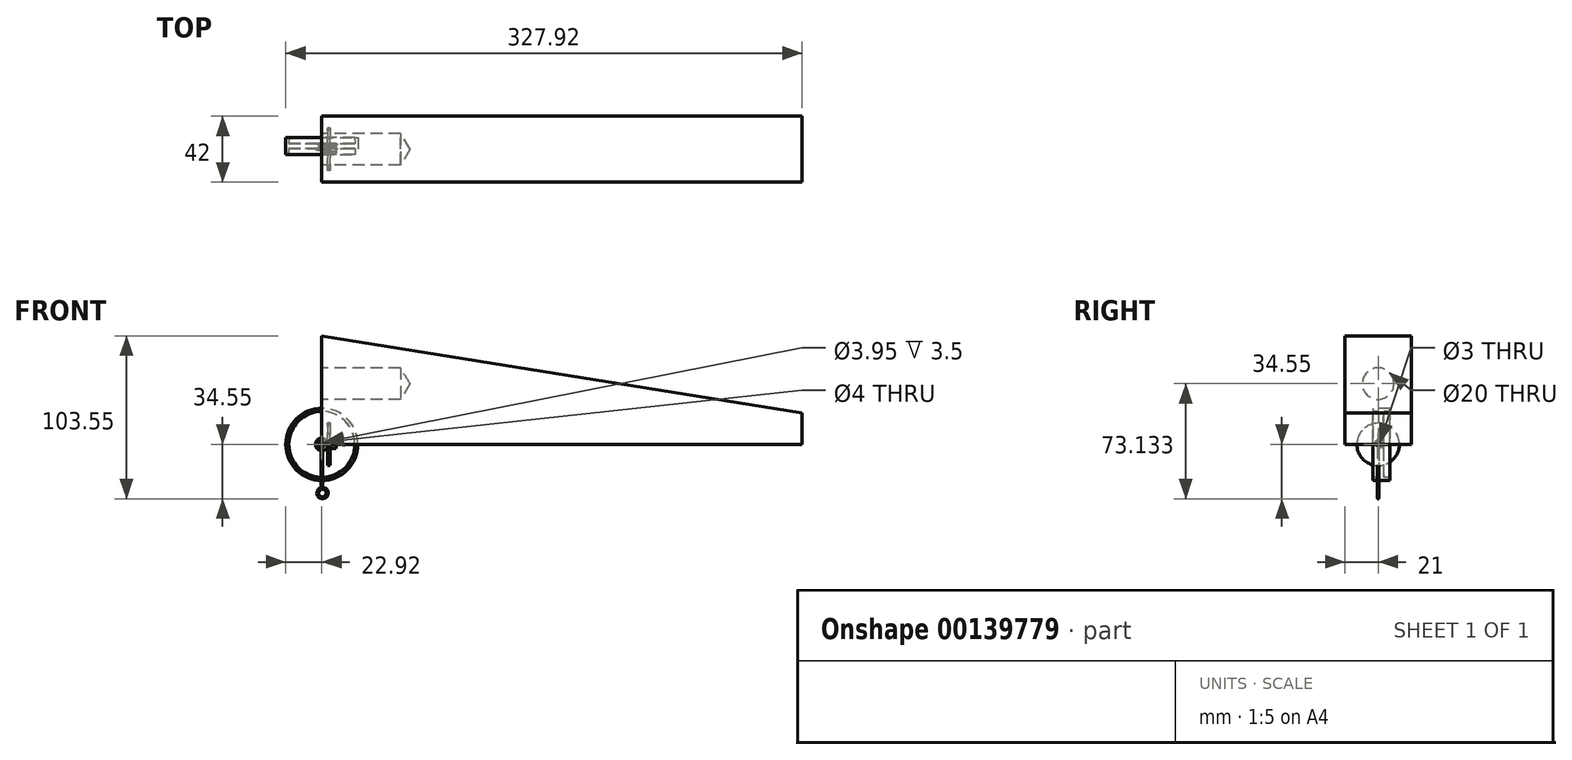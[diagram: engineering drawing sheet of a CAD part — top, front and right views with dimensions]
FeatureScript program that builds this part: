
annotation { "Feature Type Name" : "Feature", "Feature Type Description" : "" }
export const myFeature = defineFeature(function(context is Context, id is Id, definition is map)
    precondition{}
    {
        {
            var Q0;
            Q0=qCreatedBy(makeId("Front.planeOp"),FACE);
            var sketch = newSketch(context, id + "F0", { "sketchPlane" : qUnion([Q0])});
            skLineSegment(sketch, "E0", {"start": v(0, 0) * mm, "end": v(305, 0) * mm});
            skLineSegment(sketch, "E1", {"start": v(305, 0) * mm, "end": v(305, 20) * mm});
            skLineSegment(sketch, "E2", {"start": v(305, 20) * mm, "end": v(0, 69) * mm});
            skLineSegment(sketch, "E3", {"start": v(0, 69) * mm, "end": v(0, 0) * mm});
            skSolve(sketch);
        }
        {
            var Q0;
            Q0=qSketchRegion(id+"F0",true);
            extrude(context, id + "F1", {"entities" : qUnion([Q0]), "endBound" : BoundingType.SYMMETRIC, "depth" : 42 * mm});
        }
        {
            var Q0;
            Q0=qCreatedBy(makeId("Front.planeOp"),FACE);
            var sketch = newSketch(context, id + "F2", { "sketchPlane" : qUnion([Q0])});
            skCircle(sketch, "E4", {"center": v(0, 0) * mm, "radius": 4 * mm});
            skCircle(sketch, "E5", {"center": v(0, 0) * mm, "radius": 2 * mm});
            skSolve(sketch);
        }
        {
            var Q0;
            Q0=makeQuery(id+"F2.imprint","IMPRINT",FACE,{"disambiguationData":[TD([[makeQuery(id+"F2.imprint","IMPRINT",EDGE,{"derivedFrom":sQuery(id+"F2.wireOp",EDGE,"E4")}),1.0]])]});
            extrude(context, id + "F3", {"entities" : qUnion([Q0]), "endBound" : BoundingType.SYMMETRIC, "depth" : .33333333333333331968 * mm});
        }
        {
            var Q0;
            Q0=qCreatedBy(makeId("Right.planeOp"),FACE);
            var sketch = newSketch(context, id + "F4", { "sketchPlane" : qUnion([Q0])});
            skLineSegment(sketch, "E6", {"start": v(0, 0) * mm, "end": v(4.06, 0) * mm, "construction": true});
            skLineSegment(sketch, "E7", {"start": v(0, 1.98) * mm, "end": v(3.5, 1.98) * mm});
            skLineSegment(sketch, "E8", {"start": v(3.5, 1.98) * mm, "end": v(3.5, 2.98) * mm});
            skLineSegment(sketch, "E9", {"start": v(0, 1.98) * mm, "end": v(0, 2.98) * mm});
            skLineSegment(sketch, "E10", {"start": v(0, 2.98) * mm, "end": v(0.25, 2.98) * mm});
            skLineSegment(sketch, "E11", {"start": v(3.5, 2.98) * mm, "end": v(3.25, 2.98) * mm});
            skLineSegment(sketch, "E12", {"start": v(0.25, 2.98) * mm, "end": v(3.25, 2.98) * mm});
            skLineSegment(sketch, "E13", {"start": v(3.25, 2.98) * mm, "end": v(3.5, 20.97) * mm});
            skLineSegment(sketch, "E14", {"start": v(0.25, 2.98) * mm, "end": v(0.5, 20.97) * mm});
            skLineSegment(sketch, "E15", {"start": v(3.5, 20.97) * mm, "end": v(7.5, 20.92) * mm});
            skLineSegment(sketch, "E16", {"start": v(0.5, 20.97) * mm, "end": v(-3.5, 21.03) * mm});
            skLineSegment(sketch, "E17", {"start": v(7.5, 20.92) * mm, "end": v(7.53, 22.92) * mm});
            skLineSegment(sketch, "E18", {"start": v(-3.5, 21.03) * mm, "end": v(-3.5, 22.92) * mm});
            skLineSegment(sketch, "E19", {"start": v(-3.5, 22.92) * mm, "end": v(7.53, 22.92) * mm});
            skSolve(sketch);
        }
        {
            var Q0;
            Q0=qSketchRegion(id+"F4",true);
            var Q1;
            Q1=sQuery(id+"F4.wireOp",EDGE,"E6");
            revolve(context, id + "F5", {"entities" : qUnion([Q0]), "axis" : qUnion([Q1]), "revolveType" : RevolveType.FULL});
        }
        {
            var Q0;
            Q0=qCreatedBy(makeId("Front.planeOp"),FACE);
            var sketch = newSketch(context, id + "F6", { "sketchPlane" : qUnion([Q0])});
            skLineSegment(sketch, "E20", {"start": v(0, 0) * mm, "end": v(0, -27) * mm});
            skPoint(sketch, "E21.visualSharp", {"position": v(0, -33.93) * mm});
            skArc(sketch, "E21.filletArc", {"start": v(0, -27) * mm, "mid": v(0.24, -27.65) * mm, "end": v(0.85, -27.99) * mm});
            skArc(sketch, "E22", {"start": v(-0.7, -28.17) * mm, "mid": v(0.75, -33.94) * mm, "end": v(0.85, -27.99) * mm});
            skSolve(sketch);
        }
        {
            var Q0;
            Q0=qCreatedBy(makeId("Top.planeOp"),FACE);
            var sketch = newSketch(context, id + "F7", { "sketchPlane" : qUnion([Q0])});
            skCircle(sketch, "E23", {"center": v(0, 0) * mm, "radius": 0.6 * mm});
            skSolve(sketch);
        }
        {
            var Q0;
            Q0=makeQuery(id+"F7.imprint","IMPRINT",FACE,{"disambiguationData":[TD([[makeQuery(id+"F7.imprint","IMPRINT",EDGE,{"derivedFrom":sQuery(id+"F7.wireOp",EDGE,"E23")}),1.0]])]});
            var Q1;
            Q1=sQuery(id+"F6.wireOp",EDGE,"E20");
            var Q2;
            Q2=sQuery(id+"F6.wireOp",EDGE,"E21.filletArc");
            var Q3;
            Q3=sQuery(id+"F6.wireOp",EDGE,"E22");
            sweep(context, id + "F8", {"profiles" : qUnion([Q0]), "path" : qUnion([Q1, Q2, Q3])});
        }
        {
            var Q0;
            Q0=qCreatedBy(makeId("Front.planeOp"),FACE);
            var sketch = newSketch(context, id + "F9", { "sketchPlane" : qUnion([Q0])});
            skLineSegment(sketch, "E24", {"start": v(0, 0) * mm, "end": v(9.03, 0) * mm, "construction": true});
            skLineSegment(sketch, "E25", {"start": v(0, 2.5) * mm, "end": v(9, 2.5) * mm});
            skLineSegment(sketch, "E26", {"start": v(5.25, 2.5) * mm, "end": v(5.25, 13.5) * mm});
            skLineSegment(sketch, "E27", {"start": v(3.75, 2.5) * mm, "end": v(3.75, 13.5) * mm});
            skLineSegment(sketch, "E28", {"start": v(3.75, 13.5) * mm, "end": v(5.25, 13.5) * mm});
            skLineSegment(sketch, "E29", {"start": v(0, 2.5) * mm, "end": v(0, 1.5) * mm});
            skLineSegment(sketch, "E30", {"start": v(9, 2.5) * mm, "end": v(9, 1.5) * mm});
            skLineSegment(sketch, "E31", {"start": v(9, 1.5) * mm, "end": v(0, 1.5) * mm});
            skSolve(sketch);
        }
        {
            var Q0;
            {var subQ0=sQuery(id+"F9.wireOp",EDGE,"E29");Q0=makeQuery(id+"F9.imprint","IMPRINT",FACE,{"disambiguationData":[TD([[makeQuery(id+"F9.imprint","IMPRINT",EDGE,{"derivedFrom":subQ0}),1.0]])]});}
            var Q1;
            {var subQ0=sQuery(id+"F9.wireOp",EDGE,"E26");Q1=makeQuery(id+"F9.imprint","IMPRINT",FACE,{"disambiguationData":[TD([[makeQuery(id+"F9.imprint","IMPRINT",EDGE,{"derivedFrom":subQ0}),1.0]])]});}
            var Q2;
            Q2=sQuery(id+"F9.wireOp",EDGE,"E24");
            revolve(context, id + "F10", {"entities" : qUnion([Q0, Q1]), "axis" : qUnion([Q2]), "revolveType" : RevolveType.FULL});
        }
        {
            var Q0;
            Q0=makeQuery(id+"F1.opExtrude","SWEPT_FACE",FACE,{"disambiguationData":[OSD([sQuery(id+"F0.wireOp",EDGE,"E3")])]});
            var sketch = newSketch(context, id + "F11", { "sketchPlane" : qUnion([Q0])});
            skPoint(sketch, "E32", {"position": v(0, 38.58) * mm});
            skSolve(sketch);
        }
        {
            var Q0;
            Q0=sQuery(id+"F11.wireOp",VERTEX,"E32");
            var Q1;
            Q1=makeQuery(id+"F1.opExtrude","SWEPT_BODY",BODY,{"disambiguationData":[OSD([sQuery(id+"F0.wireOp",EDGE,"E0"),sQuery(id+"F0.wireOp",EDGE,"E1"),sQuery(id+"F0.wireOp",EDGE,"E2"),sQuery(id+"F0.wireOp",EDGE,"E3")])]});
            hole(context, id + "F12", {"style" : HoleStyle.SIMPLE, "endStyle" : HoleEndStyle.BLIND, "holeDiameter" : 20 * mm, "holeDepth" : 50 * mm, "locations" : qUnion([Q0]), "scope" : qUnion([Q1])});
        }
    });
